# Revit family: Shades-Hunter_Douglas-RB500-Single_Heavy_Duty-Clutch-Dual_7in_UM-Pocket
name_source: partatom
category: Specialty Equipment
units: mm (PartAtom-declared; Revit-internal decimal feet)

## family parameters
Always vertical = Yes
Classification Number = 23.30.60.14
Cut with Voids When Loaded = No
Enable Cutting in Views = No
Maintain Annotation Orientation = No
Part Type = Normal
Room Calculation Point = No
Round Connector Dimension = Use Diameter
Shared = No
Work Plane-Based = No

## types (3) — shared parameters
Assembly Code = E2010300
CD_Fabric Sizing Disclaimer = Designer to verify maximum fabric size with Manufacturer as the maximum fabric size is dependent on finished dimensions
CD_Finish = Fabric-Shade-Hunter_Douglas-5%-E_Screen-Charcoal_Cocoa
CD_Finish Frame = Metal-Aluminum-Hunter_Douglas-Anodized
CD_Finish Rail = Metal-Aluminum-Hunter_Douglas-Anodized
CD_Install Documentation = https://www.hunterdouglasarchitectural.com
CD_Microsite = https://microsite.caddetails.com
CD_Product Documentation Link = https://www.hunterdouglasarchitectural.com
CD_Product Name = RB 500 Roller Shade System
CD_Product Page URL = https://www.hunterdouglasarchitectural.com
CD_Warranty = https://assets.hunterdouglasarchitectural.com
Default Elevation = 0' - 0"
Description = Heavy Duty Clutch Roller Shade
Manufacturer = Hunter Douglas Architectural
Model = Heavy Duty Clutch Dual 7in UM
URL = https://www.hunterdouglasarchitectural.com

## per-type parameters (varying)
| type | CD_Bracket Center Line Offset | CD_Bracket Depth | CD_Bracket Height | CD_Gypsum Pocket | CD_Screen Offset From Face | CD_Surface Pocket | CD_Surface Pocket Calc | CD_Tile Pocket | Cd_Bracket Offset |
| Surface Pocket | 0' - 4 17/32" | 0' - 9" | 0' - 9" | No | 0' - 1 15/32" | Yes | Yes | No | 0' - 0 3/16" |
| Tile Pocket | 0' - 4 17/32" | 0' - 9" | 0' - 9" | No | 0' - 1 15/32" | No | Yes | Yes | 0' - 0 3/16" |
| Gypsum Pocket | 0' - 2 31/32" | 0' - 6 23/32" | 0' - 8 13/16" | Yes | 0' - 0 23/32" | No | No | No | 0' - 0" |

note: column(s) folded — value = type name in every type: Type Comments

## geometry (parser evidence)
native form markers: Sweep x3
no freeform markers — native parametric forms only
